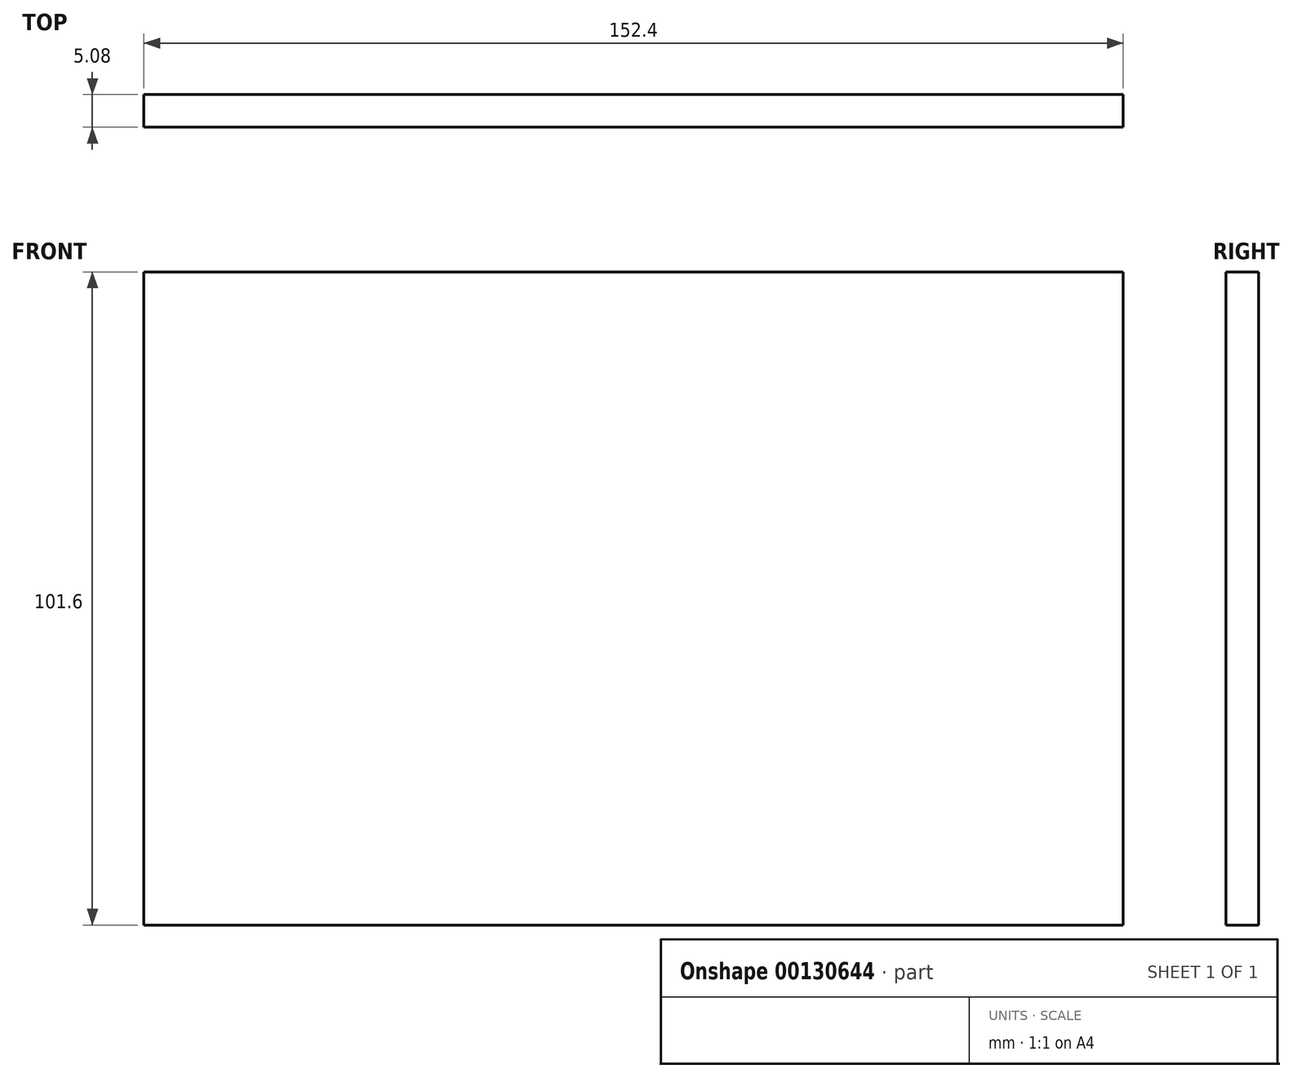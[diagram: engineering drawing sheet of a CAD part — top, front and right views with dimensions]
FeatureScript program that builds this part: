
annotation { "Feature Type Name" : "Feature", "Feature Type Description" : "" }
export const myFeature = defineFeature(function(context is Context, id is Id, definition is map)
    precondition{}
    {
        {
            var Q0;
            Q0=qCreatedBy(makeId("Front.planeOp"),FACE);
            var sketch = newSketch(context, id + "F0", { "sketchPlane" : qUnion([Q0])});
            skLineSegment(sketch, "E0.bottom", {"start": v(-65.17, 51.22) * mm, "end": v(87.23, 51.22) * mm});
            skLineSegment(sketch, "E0.top", {"start": v(-65.17, -50.38) * mm, "end": v(87.23, -50.38) * mm});
            skLineSegment(sketch, "E0.left", {"start": v(-65.17, 51.22) * mm, "end": v(-65.17, -50.38) * mm});
            skLineSegment(sketch, "E0.right", {"start": v(87.23, 51.22) * mm, "end": v(87.23, -50.38) * mm});
            skSolve(sketch);
        }
        {
            var Q0;
            Q0 = qSketchRegion(id + "F0", true);
            extrude(context, id + "F1", {"entities" : qUnion([Q0]), "depth" : 5.08 * mm});
        }
    });
